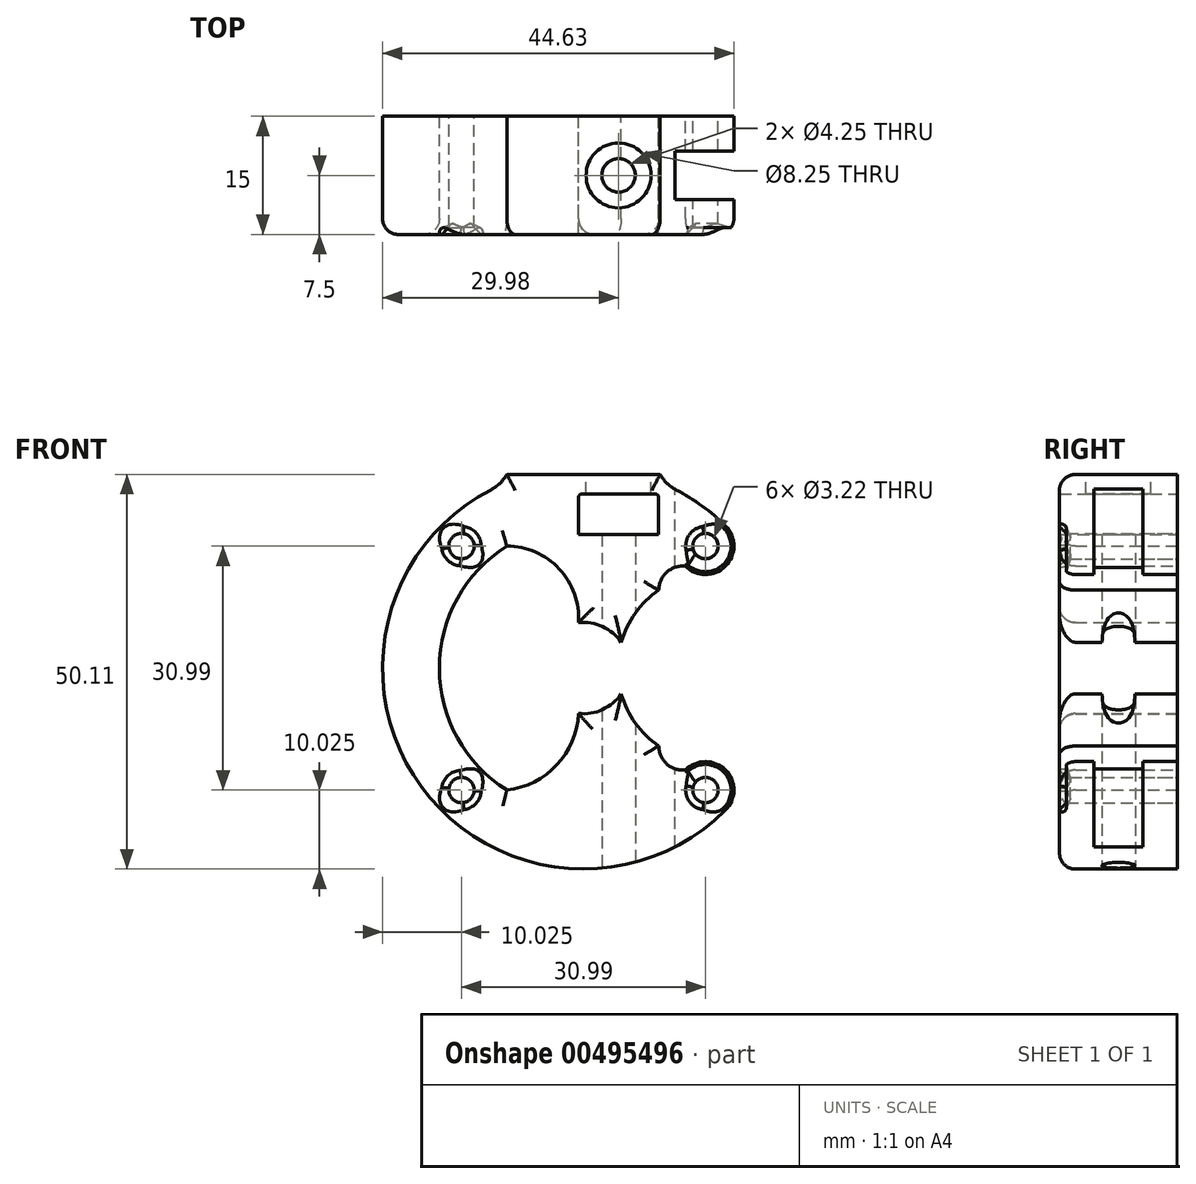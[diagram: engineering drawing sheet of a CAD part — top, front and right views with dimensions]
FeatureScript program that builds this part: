
annotation { "Feature Type Name" : "Feature", "Feature Type Description" : "" }
export const myFeature = defineFeature(function(context is Context, id is Id, definition is map)
    precondition{}
    {
        {
            var Q0;
            Q0=qCreatedBy(makeId("Front.planeOp"),FACE);
            var sketch = newSketch(context, id + "F0", { "sketchPlane" : qUnion([Q0])});
            skLineSegment(sketch, "E0.bottom", {"start": v(15.5, -15.5) * mm, "end": v(-15.5, -15.5) * mm, "construction": true});
            skLineSegment(sketch, "E0.top", {"start": v(15.5, 15.5) * mm, "end": v(-15.5, 15.5) * mm, "construction": true});
            skLineSegment(sketch, "E0.left", {"start": v(15.5, -15.5) * mm, "end": v(15.5, 15.5) * mm, "construction": true});
            skLineSegment(sketch, "E0.right", {"start": v(-15.5, -15.5) * mm, "end": v(-15.5, 15.5) * mm, "construction": true});
            skPoint(sketch, "E0.middle", {"position": v(0, 0) * mm});
            skCircle(sketch, "E1", {"center": v(-15.5, 15.5) * mm, "radius": 1.61 * mm});
            skCircle(sketch, "E2", {"center": v(15.5, 15.5) * mm, "radius": 1.61 * mm});
            skCircle(sketch, "E3", {"center": v(15.5, -15.5) * mm, "radius": 1.61 * mm});
            skCircle(sketch, "E4", {"center": v(-15.5, -15.5) * mm, "radius": 1.61 * mm});
            skArc(sketch, "E5", {"start": v(18.05, 18.05) * mm, "mid": v(14.17, 21.23) * mm, "end": v(9.74, 23.6) * mm});
            skArc(sketch, "E6", {"start": v(12.94, 12.94) * mm, "mid": v(18.05, 12.94) * mm, "end": v(18.05, 18.05) * mm});
            skArc(sketch, "E7", {"start": v(18.05, -18.05) * mm, "mid": v(18.05, -12.94) * mm, "end": v(12.94, -12.94) * mm});
            skArc(sketch, "E8.trimOffspring", {"start": v(-9.74, 15.5) * mm, "mid": v(-18.3, 0) * mm, "end": v(-9.74, -15.5) * mm});
            skLineSegment(sketch, "E9.bottom", {"start": v(-0.64, 22.14) * mm, "end": v(9.56, 22.14) * mm});
            skLineSegment(sketch, "E9.top", {"start": v(-0.64, 16.94) * mm, "end": v(9.56, 16.94) * mm});
            skLineSegment(sketch, "E9.left", {"start": v(-0.64, 22.14) * mm, "end": v(-0.64, 16.94) * mm});
            skLineSegment(sketch, "E9.right", {"start": v(9.56, 22.14) * mm, "end": v(9.56, 16.94) * mm});
            skArc(sketch, "E10.trimOffspring", {"start": v(-9.74, 23.6) * mm, "mid": v(-21.23, -14.17) * mm, "end": v(18.05, -18.05) * mm});
            skLineSegment(sketch, "E11.left", {"start": v(-0.64, 6.98) * mm, "end": v(-0.64, 5.76) * mm});
            skPoint(sketch, "E11.top.end.orphan", {"position": v(9.56, -18.78) * mm});
            skArc(sketch, "E12", {"start": v(-0.64, -5.76) * mm, "mid": v(2.42, -5.27) * mm, "end": v(4.79, -3.27) * mm});
            skArc(sketch, "E13", {"start": v(9.56, 9.9) * mm, "mid": v(6.6, 7) * mm, "end": v(4.79, 3.27) * mm});
            skArc(sketch, "E14.trimOffspring", {"start": v(4.79, -3.27) * mm, "mid": v(6.6, -7) * mm, "end": v(9.56, -9.9) * mm});
            skArc(sketch, "E15.trimOffspring", {"start": v(4.79, 3.27) * mm, "mid": v(2.42, 5.27) * mm, "end": v(-0.64, 5.76) * mm});
            skArc(sketch, "E16", {"start": v(12.94, 12.94) * mm, "mid": v(10.57, 12.18) * mm, "end": v(9.56, 9.9) * mm});
            skArc(sketch, "E17", {"start": v(-0.64, 5.76) * mm, "mid": v(-3.08, 12.6) * mm, "end": v(-9.74, 15.5) * mm});
            skPoint(sketch, "E18.orphan", {"position": v(-0.64, 15.5) * mm});
            skArc(sketch, "E19", {"start": v(9.56, -9.9) * mm, "mid": v(10.57, -12.18) * mm, "end": v(12.94, -12.94) * mm});
            skArc(sketch, "E20", {"start": v(-9.74, -15.5) * mm, "mid": v(-3.4, -12.31) * mm, "end": v(-0.64, -5.76) * mm});
            skLineSegment(sketch, "E21.top", {"start": v(-9.74, 24.6) * mm, "end": v(9.74, 24.6) * mm});
            skLineSegment(sketch, "E21.left", {"start": v(-9.74, 23.6) * mm, "end": v(-9.74, 24.6) * mm});
            skLineSegment(sketch, "E21.right", {"start": v(9.74, 23.6) * mm, "end": v(9.74, 24.6) * mm});
            skSolve(sketch);
        }
        {
            var Q0;
            Q0=makeQuery(id+"F0.imprint","IMPRINT",FACE,{"disambiguationData":[TD([[makeQuery(id+"F0.imprint","IMPRINT",EDGE,{"derivedFrom":sQuery(id+"F0.wireOp",EDGE,"E1")}),-1.0]])]});
            extrude(context, id + "F1", {"entities" : qUnion([Q0]), "depth" : 15 * mm});
        }
        {
            var Q0;
            Q0=makeQuery(id+"F1.opExtrude","SWEPT_EDGE",EDGE,{"disambiguationData":[OSD([sQuery(id+"F0.wireOp",EDGE,"E5"),sQuery(id+"F0.wireOp",EDGE,"E21.right")])]});
            var Q1;
            Q1=makeQuery(id+"F1.opExtrude","SWEPT_EDGE",EDGE,{"disambiguationData":[OSD([sQuery(id+"F0.wireOp",EDGE,"E10.trimOffspring"),sQuery(id+"F0.wireOp",EDGE,"E21.left")])]});
            fillet(context, id + "F2", {"entities" : qUnion([Q0, Q1]), "radius" : 5 * mm, "tangentPropagation" : true, "allowEdgeOverflow" : false});
        }
        {
            var Q0;
            Q0=makeQuery(id+"F1.opExtrude","SWEPT_FACE",FACE,{"disambiguationData":[OSD([sQuery(id+"F0.wireOp",EDGE,"E9.top")])]});
            var sketch = newSketch(context, id + "F3", { "sketchPlane" : qUnion([Q0])});
            skCircle(sketch, "E22", {"center": v(4.46, -7.5) * mm, "radius": 2.12 * mm});
            skPoint(sketch, "E22.centerSnap0", {"position": v(-0.64, -7.5) * mm});
            skPoint(sketch, "E22.centerSnap1", {"position": v(4.46, 0) * mm});
            skSolve(sketch);
        }
        {
            var Q0;
            Q0=makeQuery(id+"F3.imprint","IMPRINT",FACE,{"disambiguationData":[TD([[makeQuery(id+"F3.imprint","IMPRINT",EDGE,{"derivedFrom":sQuery(id+"F3.wireOp",EDGE,"E22")}),1.0]])]});
            extrude(context, id + "F4", {"entities" : qUnion([Q0]), "operationType" : NewBodyOperationType.REMOVE, "endBound" : BoundingType.THROUGH_ALL, "depth" : 60 * mm, "hasSecondDirection" : true, "secondDirectionBound" : SecondDirectionBoundingType.THROUGH_ALL, "secondDirectionOppositeDirection" : true, "secondDirectionDepth" : 25 * mm});
        }
        {
            var Q0;
            Q0=makeQuery(id+"F1.opExtrude","SWEPT_FACE",FACE,{"disambiguationData":[OSD([sQuery(id+"F0.wireOp",EDGE,"E21.top")])]});
            var sketch = newSketch(context, id + "F5", { "sketchPlane" : qUnion([Q0])});
            skCircle(sketch, "E23", {"center": v(4.46, -7.5) * mm, "radius": 4.12 * mm});
            skSolve(sketch);
        }
        {
            var Q0;
            Q0=makeQuery(id+"F5.imprint","IMPRINT",FACE,{"disambiguationData":[TD([[makeQuery(id+"F5.imprint","IMPRINT",EDGE,{"derivedFrom":sQuery(id+"F5.wireOp",EDGE,"E23")}),1.0]])]});
            var Q1;
            Q1=sQuery(id+"F5.wireOp",EDGE,"E23");
            extrude(context, id + "F6", {"entities" : qUnion([Q0]), "operationType" : NewBodyOperationType.REMOVE, "surfaceEntities" : qUnion([Q1]), "endBound" : BoundingType.UP_TO_NEXT, "oppositeDirection" : true, "depth" : 25 * mm});
        }
        {
            var Q0;
            Q0=makeQuery(id+"F1.opExtrude","CAP_EDGE",EDGE,{"disambiguationData":[OSD([sQuery(id+"F0.wireOp",EDGE,"E17")])],"isStart":false});
            var Q1;
            Q1=makeQuery(id+"F1.opExtrude","CAP_EDGE",EDGE,{"disambiguationData":[OSD([sQuery(id+"F0.wireOp",EDGE,"E8.trimOffspring")])],"isStart":false});
            var Q2;
            Q2=makeQuery(id+"F1.opExtrude","CAP_EDGE",EDGE,{"disambiguationData":[OSD([sQuery(id+"F0.wireOp",EDGE,"E15.trimOffspring")])],"isStart":false});
            var Q3;
            Q3=makeQuery(id+"F1.opExtrude","CAP_EDGE",EDGE,{"disambiguationData":[OSD([sQuery(id+"F0.wireOp",EDGE,"E13")])],"isStart":false});
            var Q4;
            Q4=makeQuery(id+"F1.opExtrude","CAP_EDGE",EDGE,{"disambiguationData":[OSD([sQuery(id+"F0.wireOp",EDGE,"E16")])],"isStart":false});
            var Q5;
            Q5=makeQuery(id+"F1.opExtrude","CAP_EDGE",EDGE,{"disambiguationData":[OSD([sQuery(id+"F0.wireOp",EDGE,"E6")])],"isStart":false});
            var Q6;
            Q6=makeQuery(id+"F1.opExtrude","CAP_EDGE",EDGE,{"disambiguationData":[OSD([sQuery(id+"F0.wireOp",EDGE,"E10.trimOffspring")])],"isStart":false});
            var Q7;
            {var subQ0=sQuery(id+"F0.wireOp",EDGE,"E21.left");var subQ1=sQuery(id+"F0.wireOp",EDGE,"E10.trimOffspring");Q7=makeQuery(id+"F2.opFillet","BLEND_EDGE",EDGE,{"blendedFrom":[makeQuery(id+"F1.opExtrude","SWEPT_EDGE",EDGE,{"disambiguationData":[OSD([subQ1,subQ0])]}),makeQuery(id+"F1.opExtrude","CAP_FACE",FACE,{"disambiguationData":[OSD([sQuery(id+"F0.wireOp",EDGE,"E1"),sQuery(id+"F0.wireOp",EDGE,"E2"),sQuery(id+"F0.wireOp",EDGE,"E3"),sQuery(id+"F0.wireOp",EDGE,"E4"),sQuery(id+"F0.wireOp",EDGE,"E5"),sQuery(id+"F0.wireOp",EDGE,"E6"),sQuery(id+"F0.wireOp",EDGE,"E7"),sQuery(id+"F0.wireOp",EDGE,"E8.trimOffspring"),sQuery(id+"F0.wireOp",EDGE,"E9.bottom"),sQuery(id+"F0.wireOp",EDGE,"E9.top"),sQuery(id+"F0.wireOp",EDGE,"E9.left"),sQuery(id+"F0.wireOp",EDGE,"E9.right"),subQ1,sQuery(id+"F0.wireOp",EDGE,"E12"),sQuery(id+"F0.wireOp",EDGE,"E13"),sQuery(id+"F0.wireOp",EDGE,"E14.trimOffspring"),sQuery(id+"F0.wireOp",EDGE,"E15.trimOffspring"),sQuery(id+"F0.wireOp",EDGE,"E16"),sQuery(id+"F0.wireOp",EDGE,"E17"),sQuery(id+"F0.wireOp",EDGE,"E19"),sQuery(id+"F0.wireOp",EDGE,"E20"),sQuery(id+"F0.wireOp",EDGE,"E21.top"),subQ0,sQuery(id+"F0.wireOp",EDGE,"E21.right")])],"isStart":false})],"blendedInto":[makeQuery(id+"F1.opExtrude","CAP_FACE",FACE,{"disambiguationData":[OSD([sQuery(id+"F0.wireOp",EDGE,"E1"),sQuery(id+"F0.wireOp",EDGE,"E2"),sQuery(id+"F0.wireOp",EDGE,"E3"),sQuery(id+"F0.wireOp",EDGE,"E4"),sQuery(id+"F0.wireOp",EDGE,"E5"),sQuery(id+"F0.wireOp",EDGE,"E6"),sQuery(id+"F0.wireOp",EDGE,"E7"),sQuery(id+"F0.wireOp",EDGE,"E8.trimOffspring"),sQuery(id+"F0.wireOp",EDGE,"E9.bottom"),sQuery(id+"F0.wireOp",EDGE,"E9.top"),sQuery(id+"F0.wireOp",EDGE,"E9.left"),sQuery(id+"F0.wireOp",EDGE,"E9.right"),subQ1,sQuery(id+"F0.wireOp",EDGE,"E12"),sQuery(id+"F0.wireOp",EDGE,"E13"),sQuery(id+"F0.wireOp",EDGE,"E14.trimOffspring"),sQuery(id+"F0.wireOp",EDGE,"E15.trimOffspring"),sQuery(id+"F0.wireOp",EDGE,"E16"),sQuery(id+"F0.wireOp",EDGE,"E17"),sQuery(id+"F0.wireOp",EDGE,"E19"),sQuery(id+"F0.wireOp",EDGE,"E20"),sQuery(id+"F0.wireOp",EDGE,"E21.top"),subQ0,sQuery(id+"F0.wireOp",EDGE,"E21.right")])],"isStart":false})]});}
            var Q8;
            Q8=makeQuery(id+"F1.opExtrude","CAP_EDGE",EDGE,{"disambiguationData":[OSD([sQuery(id+"F0.wireOp",EDGE,"E7")])],"isStart":false});
            var Q9;
            Q9=makeQuery(id+"F1.opExtrude","CAP_EDGE",EDGE,{"disambiguationData":[OSD([sQuery(id+"F0.wireOp",EDGE,"E19")])],"isStart":false});
            var Q10;
            Q10=makeQuery(id+"F1.opExtrude","CAP_EDGE",EDGE,{"disambiguationData":[OSD([sQuery(id+"F0.wireOp",EDGE,"E14.trimOffspring")])],"isStart":false});
            var Q11;
            Q11=makeQuery(id+"F1.opExtrude","CAP_EDGE",EDGE,{"disambiguationData":[OSD([sQuery(id+"F0.wireOp",EDGE,"E12")])],"isStart":false});
            var Q12;
            Q12=makeQuery(id+"F1.opExtrude","CAP_EDGE",EDGE,{"disambiguationData":[OSD([sQuery(id+"F0.wireOp",EDGE,"E20")])],"isStart":false});
            var Q13;
            Q13=makeQuery(id+"F1.opExtrude","CAP_EDGE",EDGE,{"disambiguationData":[OSD([sQuery(id+"F0.wireOp",EDGE,"E21.top")])],"isStart":false});
            fillet(context, id + "F7", {"entities" : qUnion([Q0, Q1, Q2, Q3, Q4, Q5, Q6, Q7, Q8, Q9, Q10, Q11, Q12, Q13]), "radius" : 2 * mm, "tangentPropagation" : true, "allowEdgeOverflow" : false});
        }
        {
            var Q0;
            Q0=makeQuery(id+"F1.opExtrude","CAP_EDGE",EDGE,{"disambiguationData":[OSD([sQuery(id+"F0.wireOp",EDGE,"E4")])],"isStart":false});
            var Q1;
            Q1=makeQuery(id+"F1.opExtrude","CAP_EDGE",EDGE,{"disambiguationData":[OSD([sQuery(id+"F0.wireOp",EDGE,"E1")])],"isStart":false});
            var Q2;
            Q2=makeQuery(id+"F1.opExtrude","CAP_EDGE",EDGE,{"disambiguationData":[OSD([sQuery(id+"F0.wireOp",EDGE,"E1")])],"isStart":false});
            var Q3;
            Q3=makeQuery(id+"F1.opExtrude","CAP_EDGE",EDGE,{"disambiguationData":[OSD([sQuery(id+"F0.wireOp",EDGE,"E1")])],"isStart":false});
            var Q4;
            Q4=makeQuery(id+"F1.opExtrude","CAP_EDGE",EDGE,{"disambiguationData":[OSD([sQuery(id+"F0.wireOp",EDGE,"E1")])],"isStart":false});
            var Q5;
            Q5=makeQuery(id+"F1.opExtrude","CAP_EDGE",EDGE,{"disambiguationData":[OSD([sQuery(id+"F0.wireOp",EDGE,"E2")])],"isStart":false});
            var Q6;
            Q6=makeQuery(id+"F7.opFillet","BLEND_EDGE",EDGE,{"blendedFrom":[makeQuery(id+"F1.opExtrude","CAP_EDGE",EDGE,{"disambiguationData":[OSD([sQuery(id+"F0.wireOp",EDGE,"E6")])],"isStart":false}),makeQuery(id+"F1.opExtrude","SWEPT_FACE",FACE,{"disambiguationData":[OSD([sQuery(id+"F0.wireOp",EDGE,"E2")])]})],"blendedInto":[makeQuery(id+"F1.opExtrude","SWEPT_FACE",FACE,{"disambiguationData":[OSD([sQuery(id+"F0.wireOp",EDGE,"E2")])]})]});
            var Q7;
            Q7=makeQuery(id+"F7.opFillet","BLEND_EDGE",EDGE,{"blendedFrom":[makeQuery(id+"F1.opExtrude","CAP_EDGE",EDGE,{"disambiguationData":[OSD([sQuery(id+"F0.wireOp",EDGE,"E7")])],"isStart":false}),makeQuery(id+"F1.opExtrude","SWEPT_FACE",FACE,{"disambiguationData":[OSD([sQuery(id+"F0.wireOp",EDGE,"E3")])]})],"blendedInto":[makeQuery(id+"F1.opExtrude","SWEPT_FACE",FACE,{"disambiguationData":[OSD([sQuery(id+"F0.wireOp",EDGE,"E3")])]})]});
            var Q8;
            Q8=makeQuery(id+"F1.opExtrude","CAP_EDGE",EDGE,{"disambiguationData":[OSD([sQuery(id+"F0.wireOp",EDGE,"E3")])],"isStart":false});
            chamfer(context, id + "F8", {"entities" : qUnion([Q0, Q1, Q2, Q3, Q4, Q5, Q6, Q7, Q8]), "width" : 0.9 * mm, "tangentPropagation" : true});
        }
        {
            var Q0;
            Q0=makeQuery(id+"F1.opExtrude","SWEPT_FACE",FACE,{"disambiguationData":[OSD([sQuery(id+"F0.wireOp",EDGE,"E21.top")])]});
            var sketch = newSketch(context, id + "F9", { "sketchPlane" : qUnion([Q0])});
            skLineSegment(sketch, "E24.bottom", {"start": v(11.6, -4.4) * mm, "end": v(19.1, -4.4) * mm});
            skLineSegment(sketch, "E24.top", {"start": v(11.6, -10.6) * mm, "end": v(19.1, -10.6) * mm});
            skLineSegment(sketch, "E24.left", {"start": v(11.6, -4.4) * mm, "end": v(11.6, -10.6) * mm});
            skLineSegment(sketch, "E24.right", {"start": v(19.1, -4.4) * mm, "end": v(19.1, -10.6) * mm});
            skLineSegment(sketch, "E25", {"start": v(19.1, 0.76) * mm, "end": v(19.1, -13) * mm, "construction": true});
            skLineSegment(sketch, "E26.0", {"start": v(15.16, -15) * mm, "end": v(10.85, -15) * mm, "construction": true});
            skLineSegment(sketch, "E27", {"start": v(4.46, -7.5) * mm, "end": v(22.76, -7.5) * mm, "construction": true});
            skSolve(sketch);
        }
        {
            var Q0;
            Q0=makeQuery(id+"F9.imprint","IMPRINT",FACE,{"disambiguationData":[TD([[makeQuery(id+"F9.imprint","IMPRINT",EDGE,{"derivedFrom":sQuery(id+"F9.wireOp",EDGE,"E24.bottom")}),-1.0]])]});
            extrude(context, id + "F10", {"entities" : qUnion([Q0]), "operationType" : NewBodyOperationType.REMOVE, "endBound" : BoundingType.THROUGH_ALL, "oppositeDirection" : true, "depth" : 25 * mm});
        }
        {
            var Q0;
            Q0=makeQuery(id+"F1.opExtrude","SWEPT_EDGE",EDGE,{"disambiguationData":[OSD([sQuery(id+"F0.wireOp",EDGE,"E9.bottom"),sQuery(id+"F0.wireOp",EDGE,"E9.right")])]});
            var Q1;
            Q1=makeQuery(id+"F1.opExtrude","SWEPT_EDGE",EDGE,{"disambiguationData":[OSD([sQuery(id+"F0.wireOp",EDGE,"E9.bottom"),sQuery(id+"F0.wireOp",EDGE,"E9.left")])]});
            fillet(context, id + "F11", {"entities" : qUnion([Q0, Q1]), "radius" : .5 * mm, "tangentPropagation" : true, "allowEdgeOverflow" : false});
        }
    });
